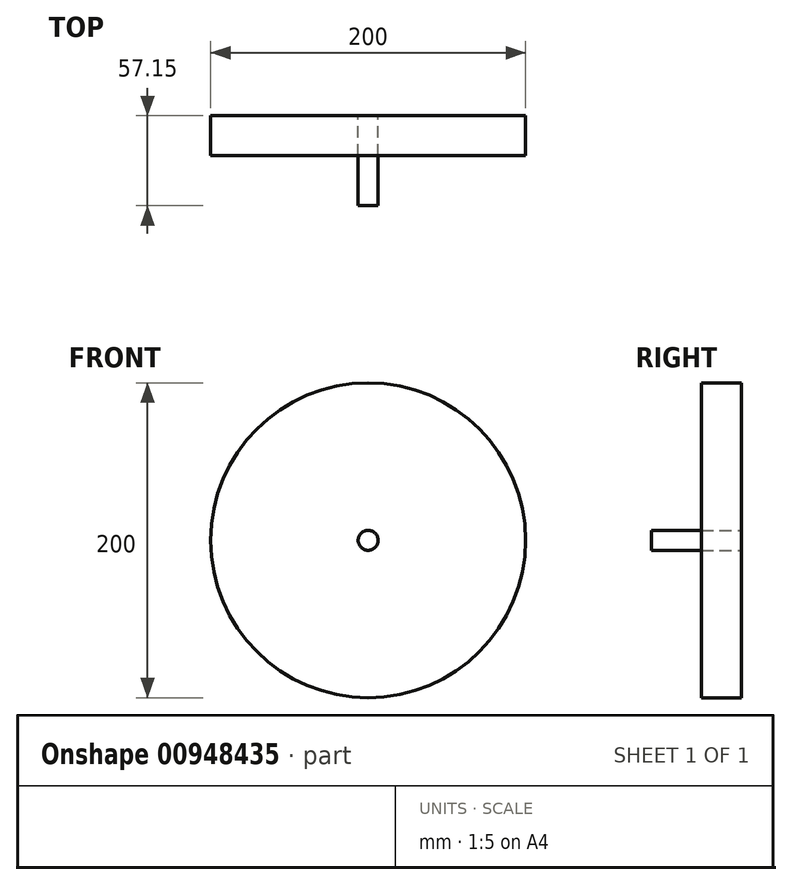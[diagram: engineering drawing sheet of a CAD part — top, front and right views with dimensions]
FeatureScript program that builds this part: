
annotation { "Feature Type Name" : "Feature", "Feature Type Description" : "" }
export const myFeature = defineFeature(function(context is Context, id is Id, definition is map)
    precondition{}
    {
        {
            var Q0;
            Q0=qCreatedBy(makeId("Front.planeOp"),FACE);
            var sketch = newSketch(context, id + "F0", { "sketchPlane" : qUnion([Q0])});
            skCircle(sketch, "E0", {"center": v(0, 0) * mm, "radius": 100 * mm});
            skCircle(sketch, "E1", {"center": v(0, 0) * mm, "radius": 6.35 * mm});
            skSolve(sketch);
        }
        {
            var Q0;
            Q0=makeQuery(id+"F0.imprint","IMPRINT",FACE,{"disambiguationData":[TD([[makeQuery(id+"F0.imprint","IMPRINT",EDGE,{"derivedFrom":sQuery(id+"F0.wireOp",EDGE,"E0")}),1.0]])]});
            var Q1;
            Q1=makeQuery(id+"F0.imprint","IMPRINT",FACE,{"disambiguationData":[TD([[makeQuery(id+"F0.imprint","IMPRINT",EDGE,{"derivedFrom":sQuery(id+"F0.wireOp",EDGE,"E1")}),1.0]])]});
            extrude(context, id + "F1", {"entities" : qUnion([Q0, Q1]), "depth" : 25.4 * mm, "offsetDistance" : 25 * mm});
        }
        {
            var Q0;
            Q0=makeQuery(id+"F0.imprint","IMPRINT",FACE,{"disambiguationData":[TD([[makeQuery(id+"F0.imprint","IMPRINT",EDGE,{"derivedFrom":sQuery(id+"F0.wireOp",EDGE,"E1")}),1.0]])]});
            var Q1;
            Q1=sQuery(id+"F0.wireOp",EDGE,"E1");
            extrude(context, id + "F2", {"entities" : qUnion([Q0]), "surfaceOperationType" : NewSurfaceOperationType.ADD, "surfaceEntities" : qUnion([Q1]), "depth" : 57.15 * mm, "offsetDistance" : 25 * mm});
        }
    });
